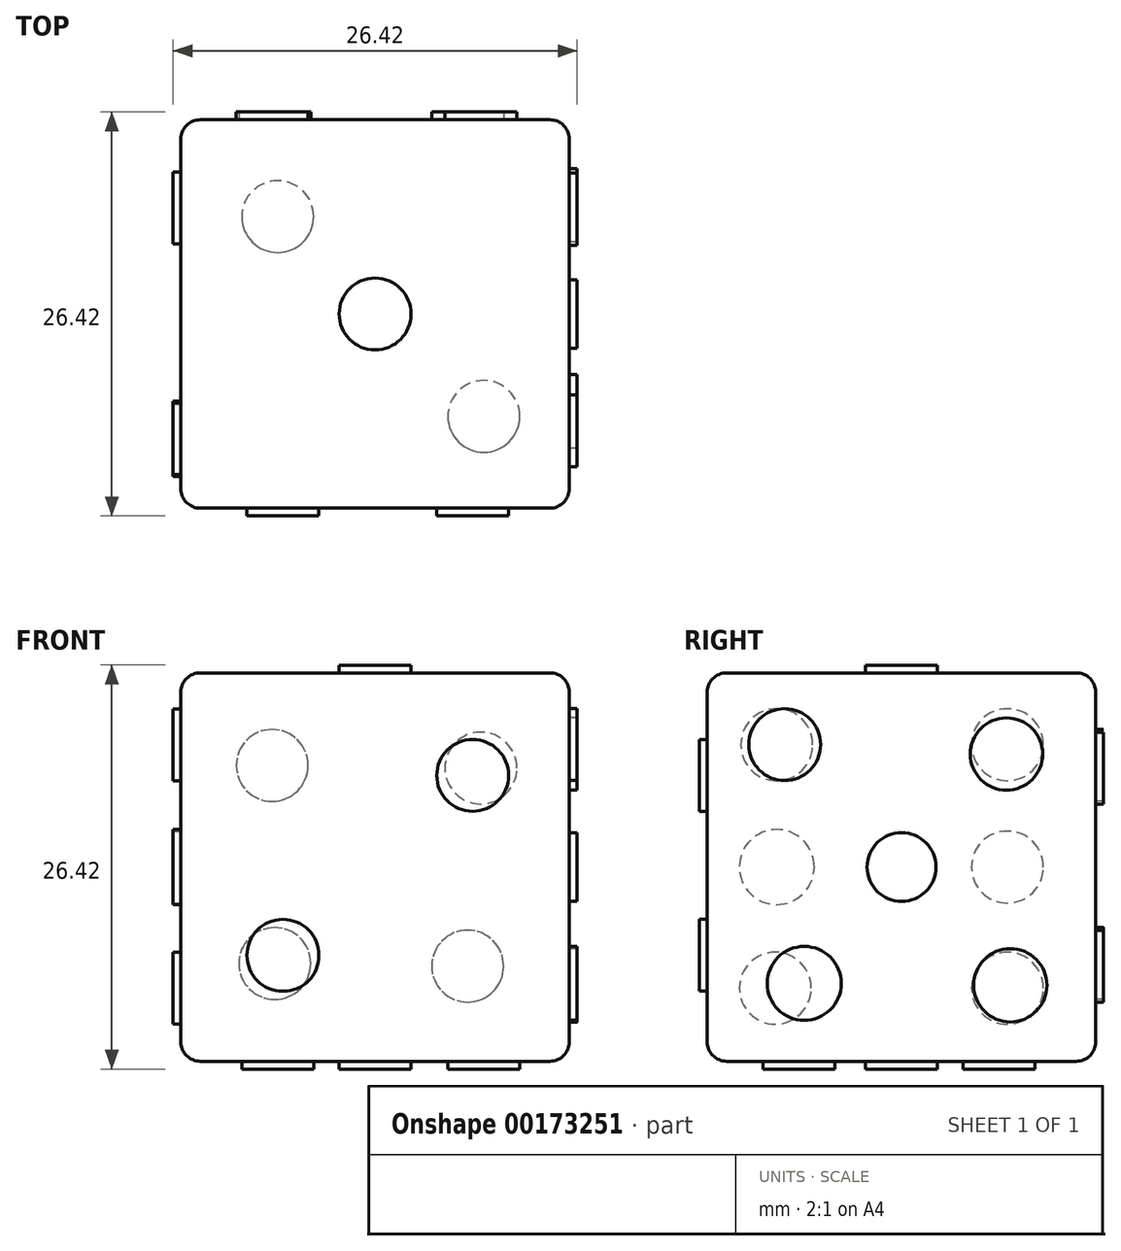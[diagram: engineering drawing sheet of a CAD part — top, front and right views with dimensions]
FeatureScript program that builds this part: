
annotation { "Feature Type Name" : "Feature", "Feature Type Description" : "" }
export const myFeature = defineFeature(function(context is Context, id is Id, definition is map)
    precondition{}
    {
        {
            var Q0;
            Q0=qCreatedBy(makeId("Top.planeOp"),FACE);
            var sketch = newSketch(context, id + "F0", { "sketchPlane" : qUnion([Q0])});
            skLineSegment(sketch, "E0.bottom", {"start": v(12.7, -12.7) * mm, "end": v(-12.7, -12.7) * mm});
            skLineSegment(sketch, "E0.top", {"start": v(12.7, 12.7) * mm, "end": v(-12.7, 12.7) * mm});
            skLineSegment(sketch, "E0.left", {"start": v(12.7, -12.7) * mm, "end": v(12.7, 12.7) * mm});
            skLineSegment(sketch, "E0.right", {"start": v(-12.7, -12.7) * mm, "end": v(-12.7, 12.7) * mm});
            skPoint(sketch, "E0.middle", {"position": v(0, 0) * mm});
            skSolve(sketch);
        }
        {
            var Q0;
            Q0=makeQuery(id+"F0.imprint","IMPRINT",FACE,{"disambiguationData":[TD([[makeQuery(id+"F0.imprint","IMPRINT",EDGE,{"derivedFrom":sQuery(id+"F0.wireOp",EDGE,"E0.bottom")}),-1.0]])]});
            extrude(context, id + "F1", {"entities" : qUnion([Q0]), "endBound" : BoundingType.SYMMETRIC, "depth" : 25.4 * mm});
        }
        {
            var Q0;
            Q0=makeQuery(id+"F1.opExtrude","CAP_FACE",FACE,{"disambiguationData":[OSD([sQuery(id+"F0.wireOp",EDGE,"E0.bottom"),sQuery(id+"F0.wireOp",EDGE,"E0.top"),sQuery(id+"F0.wireOp",EDGE,"E0.left"),sQuery(id+"F0.wireOp",EDGE,"E0.right")])],"isStart":true});
            var sketch = newSketch(context, id + "F2", { "sketchPlane" : qUnion([Q0])});
            skCircle(sketch, "E1", {"center": v(0, 0) * mm, "radius": 2.36 * mm});
            skCircle(sketch, "E2", {"center": v(7.1, 6.7) * mm, "radius": 2.35 * mm});
            skCircle(sketch, "E3", {"center": v(-6.37, -6.37) * mm, "radius": 2.35 * mm});
            skSolve(sketch);
        }
        {
            var Q0;
            Q0=makeQuery(id+"F1.opExtrude","CAP_FACE",FACE,{"disambiguationData":[OSD([sQuery(id+"F0.wireOp",EDGE,"E0.bottom"),sQuery(id+"F0.wireOp",EDGE,"E0.top"),sQuery(id+"F0.wireOp",EDGE,"E0.left"),sQuery(id+"F0.wireOp",EDGE,"E0.right")])],"isStart":false});
            var sketch = newSketch(context, id + "F3", { "sketchPlane" : qUnion([Q0])});
            skCircle(sketch, "E4", {"center": v(0, 0) * mm, "radius": 2.35 * mm});
            skSolve(sketch);
        }
        {
            var Q0;
            Q0=makeQuery(id+"F1.opExtrude","SWEPT_FACE",FACE,{"disambiguationData":[OSD([sQuery(id+"F0.wireOp",EDGE,"E0.top")])]});
            var sketch = newSketch(context, id + "F4", { "sketchPlane" : qUnion([Q0])});
            skCircle(sketch, "E5", {"center": v(-6.92, 6.47) * mm, "radius": 2.35 * mm});
            skCircle(sketch, "E6", {"center": v(6.73, 6.65) * mm, "radius": 2.35 * mm});
            skCircle(sketch, "E7", {"center": v(6.56, -6.3) * mm, "radius": 2.35 * mm});
            skCircle(sketch, "E8", {"center": v(-6.05, -6.48) * mm, "radius": 2.35 * mm});
            skSolve(sketch);
        }
        {
            var Q0;
            Q0=makeQuery(id+"F1.opExtrude","SWEPT_FACE",FACE,{"disambiguationData":[OSD([sQuery(id+"F0.wireOp",EDGE,"E0.bottom")])]});
            var sketch = newSketch(context, id + "F5", { "sketchPlane" : qUnion([Q0])});
            skCircle(sketch, "E9", {"center": v(-6.02, -5.78) * mm, "radius": 2.35 * mm});
            skCircle(sketch, "E10", {"center": v(6.38, 6) * mm, "radius": 2.35 * mm});
            skSolve(sketch);
        }
        {
            var Q0;
            Q0=makeQuery(id+"F1.opExtrude","SWEPT_FACE",FACE,{"disambiguationData":[OSD([sQuery(id+"F0.wireOp",EDGE,"E0.left")])]});
            var sketch = newSketch(context, id + "F6", { "sketchPlane" : qUnion([Q0])});
            skCircle(sketch, "E11", {"center": v(0, 0) * mm, "radius": 2.25 * mm});
            skCircle(sketch, "E12", {"center": v(7.11, -7.73) * mm, "radius": 2.4 * mm});
            skCircle(sketch, "E13", {"center": v(-6.36, -7.6) * mm, "radius": 2.42 * mm});
            skCircle(sketch, "E14", {"center": v(6.86, 7.39) * mm, "radius": 2.37 * mm});
            skCircle(sketch, "E15", {"center": v(-7.64, 8) * mm, "radius": 2.35 * mm});
            skSolve(sketch);
        }
        {
            var Q0;
            Q0=makeQuery(id+"F1.opExtrude","SWEPT_FACE",FACE,{"disambiguationData":[OSD([sQuery(id+"F0.wireOp",EDGE,"E0.right")])]});
            var sketch = newSketch(context, id + "F7", { "sketchPlane" : qUnion([Q0])});
            skCircle(sketch, "E16", {"center": v(-6.93, -7.92) * mm, "radius": 2.35 * mm});
            skCircle(sketch, "E17", {"center": v(-6.93, 8) * mm, "radius": 2.35 * mm});
            skCircle(sketch, "E18", {"center": v(8.16, 8) * mm, "radius": 2.35 * mm});
            skCircle(sketch, "E19", {"center": v(8.26, -7.92) * mm, "radius": 2.35 * mm});
            skCircle(sketch, "E20", {"center": v(-6.93, 0) * mm, "radius": 2.35 * mm});
            skCircle(sketch, "E21", {"center": v(8.16, 0) * mm, "radius": 2.45 * mm});
            skSolve(sketch);
        }
        {
            var Q0;
            Q0=makeQuery(id+"F6.imprint","IMPRINT",FACE,{"disambiguationData":[TD([[makeQuery(id+"F6.imprint","IMPRINT",EDGE,{"derivedFrom":sQuery(id+"F6.wireOp",EDGE,"E14")}),1.0]])]});
            var Q1;
            Q1=makeQuery(id+"F6.imprint","IMPRINT",FACE,{"disambiguationData":[TD([[makeQuery(id+"F6.imprint","IMPRINT",EDGE,{"derivedFrom":sQuery(id+"F6.wireOp",EDGE,"E12")}),1.0]])]});
            var Q2;
            Q2=makeQuery(id+"F6.imprint","IMPRINT",FACE,{"disambiguationData":[TD([[makeQuery(id+"F6.imprint","IMPRINT",EDGE,{"derivedFrom":sQuery(id+"F6.wireOp",EDGE,"E13")}),1.0]])]});
            var Q3;
            Q3=makeQuery(id+"F6.imprint","IMPRINT",FACE,{"disambiguationData":[TD([[makeQuery(id+"F6.imprint","IMPRINT",EDGE,{"derivedFrom":sQuery(id+"F6.wireOp",EDGE,"E11")}),1.0]])]});
            var Q4;
            Q4=makeQuery(id+"F6.imprint","IMPRINT",FACE,{"disambiguationData":[TD([[makeQuery(id+"F6.imprint","IMPRINT",EDGE,{"derivedFrom":sQuery(id+"F6.wireOp",EDGE,"E15")}),1.0]])]});
            var Q5;
            Q5=sQuery(id+"F6.wireOp",EDGE,"E14");
            extrude(context, id + "F8", {"entities" : qUnion([Q0, Q1, Q2, Q3, Q4]), "operationType" : NewBodyOperationType.ADD, "surfaceEntities" : qUnion([Q5]), "depth" : 0.5 * mm});
        }
        {
            var Q0;
            Q0=makeQuery(id+"F3.imprint","IMPRINT",FACE,{"disambiguationData":[TD([[makeQuery(id+"F3.imprint","IMPRINT",EDGE,{"derivedFrom":sQuery(id+"F3.wireOp",EDGE,"E4")}),1.0]])]});
            extrude(context, id + "F9", {"entities" : qUnion([Q0]), "operationType" : NewBodyOperationType.ADD, "depth" : 0.5 * mm});
        }
        {
            var Q0;
            Q0=makeQuery(id+"F4.imprint","IMPRINT",FACE,{"disambiguationData":[TD([[makeQuery(id+"F4.imprint","IMPRINT",EDGE,{"derivedFrom":sQuery(id+"F4.wireOp",EDGE,"E5")}),1.0]])]});
            var Q1;
            Q1=makeQuery(id+"F4.imprint","IMPRINT",FACE,{"disambiguationData":[TD([[makeQuery(id+"F4.imprint","IMPRINT",EDGE,{"derivedFrom":sQuery(id+"F4.wireOp",EDGE,"E6")}),1.0]])]});
            var Q2;
            Q2=makeQuery(id+"F4.imprint","IMPRINT",FACE,{"disambiguationData":[TD([[makeQuery(id+"F4.imprint","IMPRINT",EDGE,{"derivedFrom":sQuery(id+"F4.wireOp",EDGE,"E7")}),1.0]])]});
            var Q3;
            Q3=makeQuery(id+"F4.imprint","IMPRINT",FACE,{"disambiguationData":[TD([[makeQuery(id+"F4.imprint","IMPRINT",EDGE,{"derivedFrom":sQuery(id+"F4.wireOp",EDGE,"E8")}),1.0]])]});
            extrude(context, id + "F10", {"entities" : qUnion([Q0, Q1, Q2, Q3]), "operationType" : NewBodyOperationType.ADD, "depth" : 0.5 * mm});
        }
        {
            var Q0;
            Q0=makeQuery(id+"F5.imprint","IMPRINT",FACE,{"disambiguationData":[TD([[makeQuery(id+"F5.imprint","IMPRINT",EDGE,{"derivedFrom":sQuery(id+"F5.wireOp",EDGE,"E10")}),1.0]])]});
            extrude(context, id + "F11", {"entities" : qUnion([Q0]), "operationType" : NewBodyOperationType.ADD, "oppositeDirection" : true, "depth" : 0.5 * mm});
        }
        {
            var Q0;
            Q0=makeQuery(id+"F7.imprint","IMPRINT",FACE,{"disambiguationData":[TD([[makeQuery(id+"F7.imprint","IMPRINT",EDGE,{"derivedFrom":sQuery(id+"F7.wireOp",EDGE,"E17")}),1.0]])]});
            var Q1;
            Q1=makeQuery(id+"F7.imprint","IMPRINT",FACE,{"disambiguationData":[TD([[makeQuery(id+"F7.imprint","IMPRINT",EDGE,{"derivedFrom":sQuery(id+"F7.wireOp",EDGE,"E20")}),1.0]])]});
            var Q2;
            Q2=makeQuery(id+"F7.imprint","IMPRINT",FACE,{"disambiguationData":[TD([[makeQuery(id+"F7.imprint","IMPRINT",EDGE,{"derivedFrom":sQuery(id+"F7.wireOp",EDGE,"E16")}),1.0]])]});
            var Q3;
            Q3=makeQuery(id+"F7.imprint","IMPRINT",FACE,{"disambiguationData":[TD([[makeQuery(id+"F7.imprint","IMPRINT",EDGE,{"derivedFrom":sQuery(id+"F7.wireOp",EDGE,"E18")}),1.0]])]});
            var Q4;
            Q4=makeQuery(id+"F7.imprint","IMPRINT",FACE,{"disambiguationData":[TD([[makeQuery(id+"F7.imprint","IMPRINT",EDGE,{"derivedFrom":sQuery(id+"F7.wireOp",EDGE,"E21")}),1.0]])]});
            var Q5;
            Q5=makeQuery(id+"F7.imprint","IMPRINT",FACE,{"disambiguationData":[TD([[makeQuery(id+"F7.imprint","IMPRINT",EDGE,{"derivedFrom":sQuery(id+"F7.wireOp",EDGE,"E19")}),1.0]])]});
            extrude(context, id + "F12", {"entities" : qUnion([Q0, Q1, Q2, Q3, Q4, Q5]), "operationType" : NewBodyOperationType.ADD, "depth" : 0.5 * mm});
        }
        {
            var Q0;
            Q0=makeQuery(id+"F2.imprint","IMPRINT",FACE,{"disambiguationData":[TD([[makeQuery(id+"F2.imprint","IMPRINT",EDGE,{"derivedFrom":sQuery(id+"F2.wireOp",EDGE,"E1")}),1.0]])]});
            var Q1;
            Q1=makeQuery(id+"F2.imprint","IMPRINT",FACE,{"disambiguationData":[TD([[makeQuery(id+"F2.imprint","IMPRINT",EDGE,{"derivedFrom":sQuery(id+"F2.wireOp",EDGE,"E3")}),1.0]])]});
            var Q2;
            Q2=makeQuery(id+"F2.imprint","IMPRINT",FACE,{"disambiguationData":[TD([[makeQuery(id+"F2.imprint","IMPRINT",EDGE,{"derivedFrom":sQuery(id+"F2.wireOp",EDGE,"E2")}),1.0]])]});
            extrude(context, id + "F13", {"entities" : qUnion([Q0, Q1, Q2]), "operationType" : NewBodyOperationType.ADD, "depth" : 0.5 * mm});
        }
        {
            var Q0;
            Q0 = qSketchRegion(id + "F5", true);
            extrude(context, id + "F14", {"entities" : qUnion([Q0]), "operationType" : NewBodyOperationType.ADD, "depth" : 0.5 * mm});
        }
        {
            var Q0;
            Q0=makeQuery(id+"F1.opExtrude","CAP_EDGE",EDGE,{"disambiguationData":[OSD([sQuery(id+"F0.wireOp",EDGE,"E0.left")])],"isStart":false});
            var Q1;
            Q1=makeQuery(id+"F1.opExtrude","SWEPT_EDGE",EDGE,{"disambiguationData":[OSD([sQuery(id+"F0.wireOp",EDGE,"E0.bottom"),sQuery(id+"F0.wireOp",EDGE,"E0.left")])]});
            var Q2;
            Q2=makeQuery(id+"F1.opExtrude","CAP_EDGE",EDGE,{"disambiguationData":[OSD([sQuery(id+"F0.wireOp",EDGE,"E0.bottom")])],"isStart":false});
            var Q3;
            Q3=makeQuery(id+"F1.opExtrude","SWEPT_EDGE",EDGE,{"disambiguationData":[OSD([sQuery(id+"F0.wireOp",EDGE,"E0.bottom"),sQuery(id+"F0.wireOp",EDGE,"E0.right")])]});
            var Q4;
            Q4=makeQuery(id+"F1.opExtrude","CAP_EDGE",EDGE,{"disambiguationData":[OSD([sQuery(id+"F0.wireOp",EDGE,"E0.right")])],"isStart":false});
            var Q5;
            Q5=makeQuery(id+"F1.opExtrude","SWEPT_EDGE",EDGE,{"disambiguationData":[OSD([sQuery(id+"F0.wireOp",EDGE,"E0.top"),sQuery(id+"F0.wireOp",EDGE,"E0.right")])]});
            var Q6;
            Q6=makeQuery(id+"F1.opExtrude","CAP_EDGE",EDGE,{"disambiguationData":[OSD([sQuery(id+"F0.wireOp",EDGE,"E0.right")])],"isStart":true});
            var Q7;
            Q7=makeQuery(id+"F1.opExtrude","CAP_EDGE",EDGE,{"disambiguationData":[OSD([sQuery(id+"F0.wireOp",EDGE,"E0.top")])],"isStart":false});
            var Q8;
            Q8=makeQuery(id+"F1.opExtrude","SWEPT_EDGE",EDGE,{"disambiguationData":[OSD([sQuery(id+"F0.wireOp",EDGE,"E0.top"),sQuery(id+"F0.wireOp",EDGE,"E0.left")])]});
            var Q9;
            Q9=makeQuery(id+"F1.opExtrude","CAP_EDGE",EDGE,{"disambiguationData":[OSD([sQuery(id+"F0.wireOp",EDGE,"E0.bottom")])],"isStart":true});
            var Q10;
            Q10=makeQuery(id+"F1.opExtrude","CAP_EDGE",EDGE,{"disambiguationData":[OSD([sQuery(id+"F0.wireOp",EDGE,"E0.left")])],"isStart":true});
            var Q11;
            Q11=makeQuery(id+"F1.opExtrude","CAP_EDGE",EDGE,{"disambiguationData":[OSD([sQuery(id+"F0.wireOp",EDGE,"E0.top")])],"isStart":true});
            fillet(context, id + "F15", {"entities" : qUnion([Q0, Q1, Q2, Q3, Q4, Q5, Q6, Q7, Q8, Q9, Q10, Q11]), "radius" : 1.27 * mm, "tangentPropagation" : true, "allowEdgeOverflow" : false});
        }
    });
